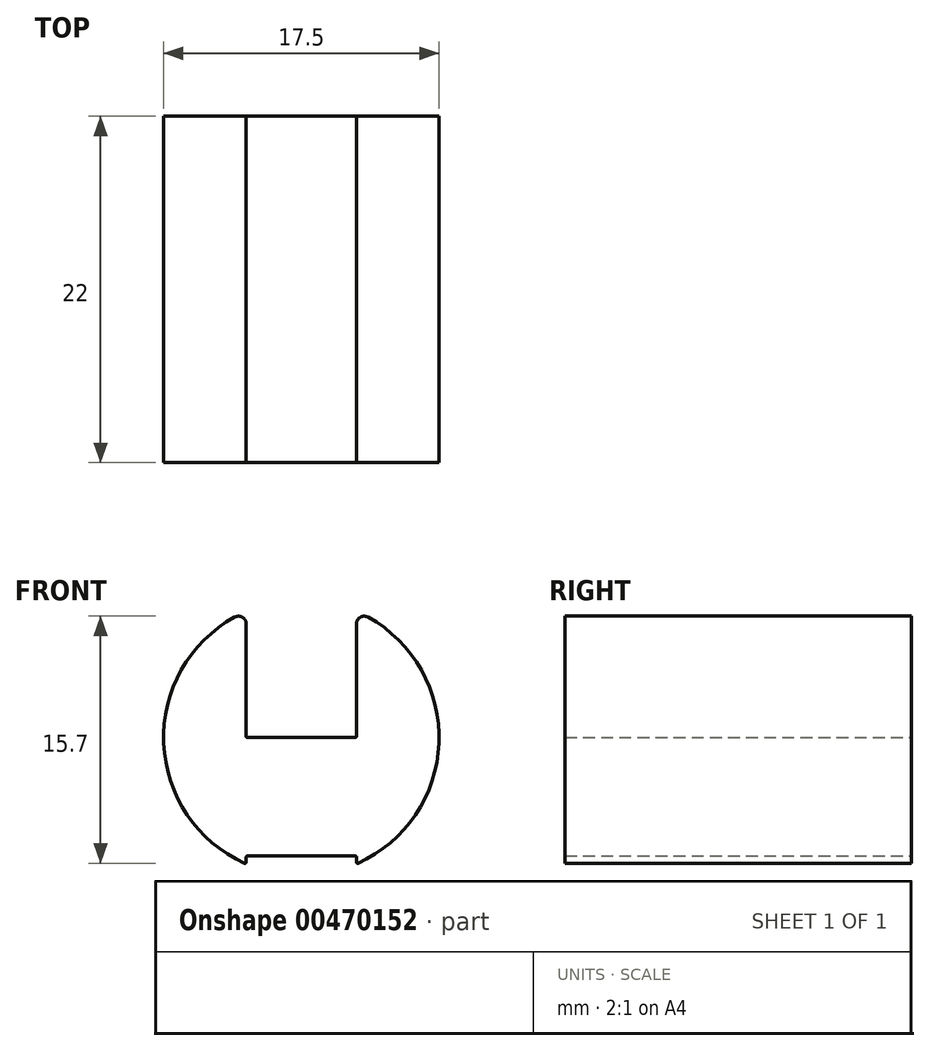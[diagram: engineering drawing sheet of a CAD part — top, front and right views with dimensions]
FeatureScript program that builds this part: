
annotation { "Feature Type Name" : "Feature", "Feature Type Description" : "" }
export const myFeature = defineFeature(function(context is Context, id is Id, definition is map)
    precondition{}
    {
        {
            var Q0;
            Q0=qCreatedBy(makeId("Front.planeOp"),FACE);
            var sketch = newSketch(context, id + "F0", { "sketchPlane" : qUnion([Q0])});
            skArc(sketch, "E0", {"start": v(-4.24, 7.65) * mm, "mid": v(-8.74, -0.36) * mm, "end": v(-3.6, -7.97) * mm});
            skLineSegment(sketch, "E1", {"start": v(-3.5, 7.22) * mm, "end": v(-3.5, 0.07) * mm});
            skLineSegment(sketch, "E2", {"start": v(-3.43, 0) * mm, "end": v(3.43, 0) * mm});
            skLineSegment(sketch, "E3", {"start": v(3.5, 0.07) * mm, "end": v(3.5, 7.22) * mm});
            skLineSegment(sketch, "E4", {"start": v(-3.5, -7.9) * mm, "end": v(-3.5, -7.6) * mm});
            skLineSegment(sketch, "E5", {"start": v(-3.43, -7.52) * mm, "end": v(3.43, -7.52) * mm});
            skLineSegment(sketch, "E6", {"start": v(3.5, -7.6) * mm, "end": v(3.5, -7.9) * mm});
            skArc(sketch, "E7.trimOffspring", {"start": v(3.6, -7.97) * mm, "mid": v(8.74, -0.36) * mm, "end": v(4.24, 7.65) * mm});
            skPoint(sketch, "E8.visualSharp", {"position": v(-3.5, 8.02) * mm});
            skArc(sketch, "E8.filletArc", {"start": v(-3.5, 7.22) * mm, "mid": v(-3.75, 7.65) * mm, "end": v(-4.24, 7.65) * mm});
            skPoint(sketch, "E9.visualSharp", {"position": v(3.5, 8.02) * mm});
            skArc(sketch, "E9.filletArc", {"start": v(4.24, 7.65) * mm, "mid": v(3.75, 7.65) * mm, "end": v(3.5, 7.22) * mm});
            skPoint(sketch, "E10.visualSharp", {"position": v(3.5, 0) * mm});
            skArc(sketch, "E10.filletArc", {"start": v(3.43, 0) * mm, "mid": v(3.48, 0.02) * mm, "end": v(3.5, 0.07) * mm});
            skPoint(sketch, "E11.visualSharp", {"position": v(-3.5, 0) * mm});
            skArc(sketch, "E11.filletArc", {"start": v(-3.5, 0.07) * mm, "mid": v(-3.48, 0.02) * mm, "end": v(-3.43, 0) * mm});
            skPoint(sketch, "E12.visualSharp", {"position": v(-3.5, -7.52) * mm});
            skArc(sketch, "E12.filletArc", {"start": v(-3.43, -7.52) * mm, "mid": v(-3.48, -7.54) * mm, "end": v(-3.5, -7.6) * mm});
            skPoint(sketch, "E13.visualSharp", {"position": v(-3.5, -8.02) * mm});
            skArc(sketch, "E13.filletArc", {"start": v(-3.6, -7.97) * mm, "mid": v(-3.53, -7.97) * mm, "end": v(-3.5, -7.9) * mm});
            skPoint(sketch, "E14.visualSharp", {"position": v(3.5, -7.52) * mm});
            skArc(sketch, "E14.filletArc", {"start": v(3.5, -7.6) * mm, "mid": v(3.48, -7.54) * mm, "end": v(3.43, -7.52) * mm});
            skPoint(sketch, "E15.visualSharp", {"position": v(3.5, -8.02) * mm});
            skArc(sketch, "E15.filletArc", {"start": v(3.5, -7.9) * mm, "mid": v(3.53, -7.97) * mm, "end": v(3.6, -7.97) * mm});
            skSolve(sketch);
        }
        {
            var Q0;
            Q0 = qSketchRegion(id + "F0", true);
            extrude(context, id + "F1", {"entities" : qUnion([Q0]), "depth" : 22 * mm});
        }
    });
